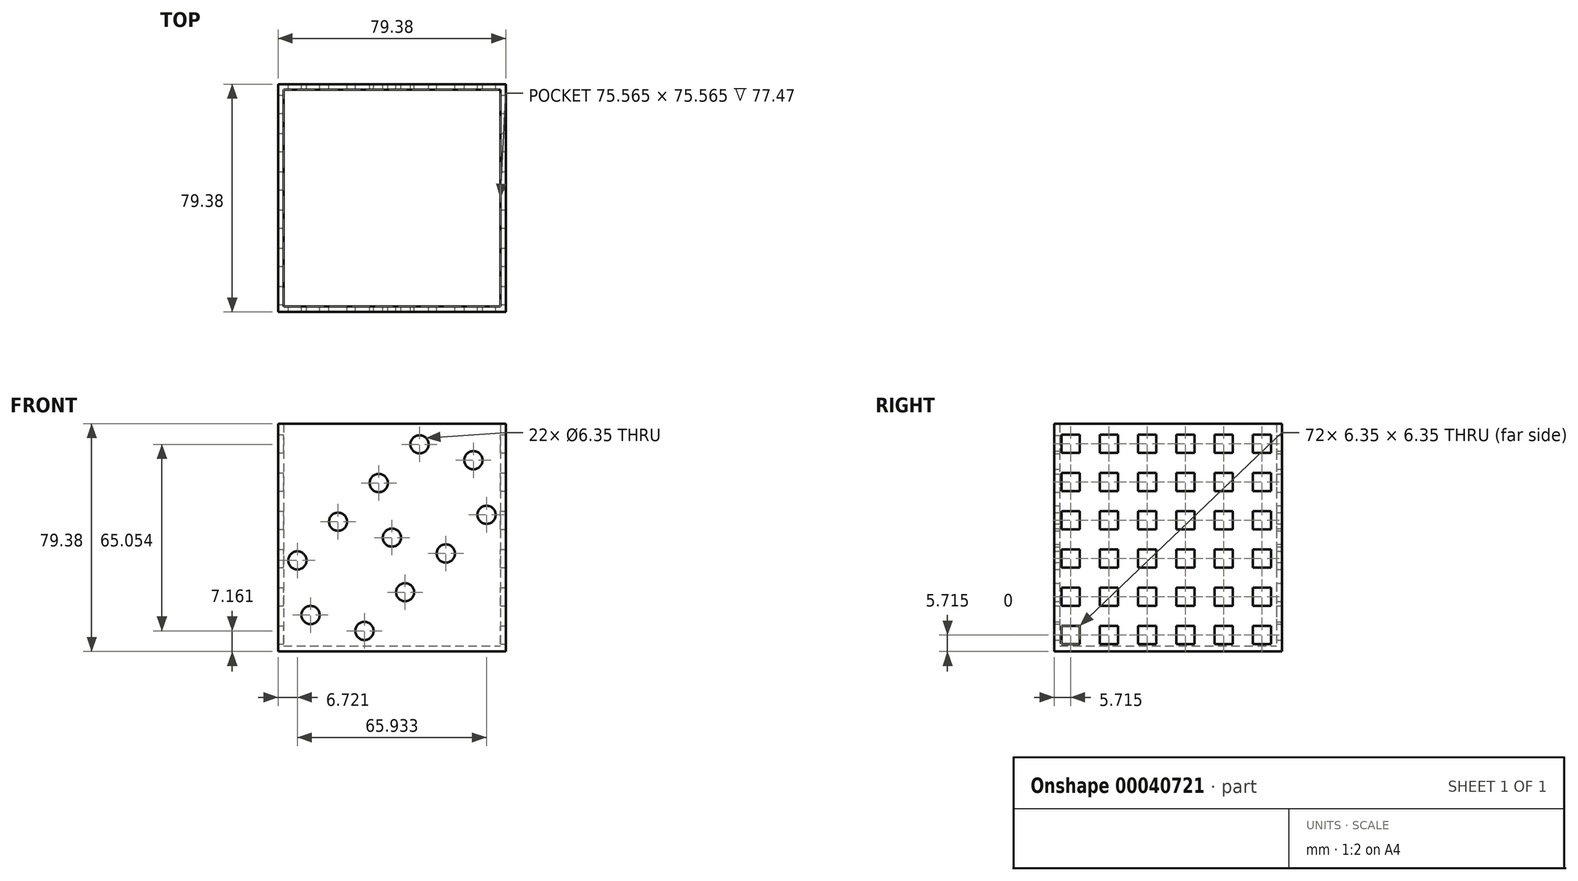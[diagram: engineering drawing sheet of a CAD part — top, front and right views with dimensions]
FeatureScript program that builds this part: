
annotation { "Feature Type Name" : "Feature", "Feature Type Description" : "" }
export const myFeature = defineFeature(function(context is Context, id is Id, definition is map)
    precondition{}
    {
        {
            var Q0;
            Q0=qCreatedBy(makeId("Top.planeOp"),FACE);
            var sketch = newSketch(context, id + "F0", { "sketchPlane" : qUnion([Q0])});
            skLineSegment(sketch, "E0.bottom", {"start": v(0, 0) * mm, "end": v(79.38, 0) * mm});
            skLineSegment(sketch, "E0.top", {"start": v(0, 79.38) * mm, "end": v(79.37, 79.38) * mm});
            skLineSegment(sketch, "E0.left", {"start": v(0, 0) * mm, "end": v(0, 79.38) * mm});
            skLineSegment(sketch, "E0.right", {"start": v(79.38, 0) * mm, "end": v(79.38, 79.38) * mm});
            skSolve(sketch);
        }
        {
            var Q0;
            Q0=makeQuery(id+"F0.imprint","IMPRINT",FACE,{"disambiguationData":[TD([[makeQuery(id+"F0.imprint","IMPRINT",EDGE,{"derivedFrom":sQuery(id+"F0.wireOp",EDGE,"E0.bottom")}),1.0]])]});
            extrude(context, id + "F1", {"entities" : qUnion([Q0]), "depth" : 79.38 * mm});
        }
        {
            var Q0;
            Q0=makeQuery(id+"F1.opExtrude","CAP_FACE",FACE,{"disambiguationData":[OSD([sQuery(id+"F0.wireOp",EDGE,"E0.bottom"),sQuery(id+"F0.wireOp",EDGE,"E0.top"),sQuery(id+"F0.wireOp",EDGE,"E0.left"),sQuery(id+"F0.wireOp",EDGE,"E0.right")])],"isStart":false});
            shell(context, id + "F2", {"entities" : qUnion([Q0]), "thickness" : 1.9 * mm});
        }
        {
            var Q0;
            Q0=makeQuery(id+"F1.opExtrude","SWEPT_FACE",FACE,{"disambiguationData":[OSD([sQuery(id+"F0.wireOp",EDGE,"E0.right")])]});
            var sketch = newSketch(context, id + "F3", { "sketchPlane" : qUnion([Q0])});
            skLineSegment(sketch, "E1.bottom", {"start": v(2.54, 8.9) * mm, "end": v(8.9, 8.9) * mm});
            skLineSegment(sketch, "E1.top", {"start": v(2.54, 2.54) * mm, "end": v(8.9, 2.54) * mm});
            skLineSegment(sketch, "E1.left", {"start": v(2.54, 8.9) * mm, "end": v(2.54, 2.54) * mm});
            skLineSegment(sketch, "E1.right", {"start": v(8.9, 8.9) * mm, "end": v(8.9, 2.54) * mm});
            skLineSegment(sketch, "E2.0.1.0", {"start": v(2.54, 22.23) * mm, "end": v(8.9, 22.23) * mm});
            skLineSegment(sketch, "E2.0.1.1", {"start": v(2.54, 22.23) * mm, "end": v(2.54, 15.88) * mm});
            skLineSegment(sketch, "E2.0.1.2", {"start": v(2.54, 15.88) * mm, "end": v(8.9, 15.88) * mm});
            skLineSegment(sketch, "E2.0.1.3", {"start": v(8.9, 22.23) * mm, "end": v(8.9, 15.88) * mm});
            skLineSegment(sketch, "E2.0.2.0", {"start": v(2.54, 35.56) * mm, "end": v(8.9, 35.56) * mm});
            skLineSegment(sketch, "E2.0.2.1", {"start": v(2.54, 35.56) * mm, "end": v(2.54, 29.21) * mm});
            skLineSegment(sketch, "E2.0.2.2", {"start": v(2.54, 29.21) * mm, "end": v(8.9, 29.21) * mm});
            skLineSegment(sketch, "E2.0.2.3", {"start": v(8.9, 35.56) * mm, "end": v(8.9, 29.21) * mm});
            skLineSegment(sketch, "E2.0.3.0", {"start": v(2.54, 48.9) * mm, "end": v(8.9, 48.9) * mm});
            skLineSegment(sketch, "E2.0.3.1", {"start": v(2.54, 48.9) * mm, "end": v(2.54, 42.55) * mm});
            skLineSegment(sketch, "E2.0.3.2", {"start": v(2.54, 42.55) * mm, "end": v(8.9, 42.55) * mm});
            skLineSegment(sketch, "E2.0.3.3", {"start": v(8.9, 48.9) * mm, "end": v(8.9, 42.55) * mm});
            skLineSegment(sketch, "E2.0.4.0", {"start": v(2.54, 62.23) * mm, "end": v(8.9, 62.23) * mm});
            skLineSegment(sketch, "E2.0.4.1", {"start": v(2.54, 62.23) * mm, "end": v(2.54, 55.88) * mm});
            skLineSegment(sketch, "E2.0.4.2", {"start": v(2.54, 55.88) * mm, "end": v(8.9, 55.88) * mm});
            skLineSegment(sketch, "E2.0.4.3", {"start": v(8.9, 62.23) * mm, "end": v(8.9, 55.88) * mm});
            skLineSegment(sketch, "E2.0.5.0", {"start": v(2.54, 75.56) * mm, "end": v(8.9, 75.56) * mm});
            skLineSegment(sketch, "E2.0.5.1", {"start": v(2.54, 75.56) * mm, "end": v(2.54, 69.22) * mm});
            skLineSegment(sketch, "E2.0.5.2", {"start": v(2.54, 69.22) * mm, "end": v(8.9, 69.22) * mm});
            skLineSegment(sketch, "E2.0.5.3", {"start": v(8.9, 75.56) * mm, "end": v(8.9, 69.22) * mm});
            skLineSegment(sketch, "E2.1.0.0", {"start": v(15.88, 8.9) * mm, "end": v(22.23, 8.9) * mm});
            skLineSegment(sketch, "E2.1.0.1", {"start": v(15.88, 8.9) * mm, "end": v(15.88, 2.54) * mm});
            skLineSegment(sketch, "E2.1.0.2", {"start": v(15.88, 2.54) * mm, "end": v(22.23, 2.54) * mm});
            skLineSegment(sketch, "E2.1.0.3", {"start": v(22.23, 8.9) * mm, "end": v(22.23, 2.54) * mm});
            skLineSegment(sketch, "E2.1.1.0", {"start": v(15.88, 22.23) * mm, "end": v(22.23, 22.23) * mm});
            skLineSegment(sketch, "E2.1.1.1", {"start": v(15.88, 22.23) * mm, "end": v(15.88, 15.88) * mm});
            skLineSegment(sketch, "E2.1.1.2", {"start": v(15.88, 15.88) * mm, "end": v(22.23, 15.88) * mm});
            skLineSegment(sketch, "E2.1.1.3", {"start": v(22.23, 22.23) * mm, "end": v(22.23, 15.88) * mm});
            skLineSegment(sketch, "E2.1.2.0", {"start": v(15.88, 35.56) * mm, "end": v(22.23, 35.56) * mm});
            skLineSegment(sketch, "E2.1.2.1", {"start": v(15.88, 35.56) * mm, "end": v(15.88, 29.21) * mm});
            skLineSegment(sketch, "E2.1.2.2", {"start": v(15.88, 29.21) * mm, "end": v(22.23, 29.21) * mm});
            skLineSegment(sketch, "E2.1.2.3", {"start": v(22.23, 35.56) * mm, "end": v(22.23, 29.21) * mm});
            skLineSegment(sketch, "E2.1.3.0", {"start": v(15.88, 48.9) * mm, "end": v(22.23, 48.9) * mm});
            skLineSegment(sketch, "E2.1.3.1", {"start": v(15.88, 48.9) * mm, "end": v(15.88, 42.55) * mm});
            skLineSegment(sketch, "E2.1.3.2", {"start": v(15.88, 42.55) * mm, "end": v(22.23, 42.55) * mm});
            skLineSegment(sketch, "E2.1.3.3", {"start": v(22.23, 48.9) * mm, "end": v(22.23, 42.55) * mm});
            skLineSegment(sketch, "E2.1.4.0", {"start": v(15.88, 62.23) * mm, "end": v(22.23, 62.23) * mm});
            skLineSegment(sketch, "E2.1.4.1", {"start": v(15.88, 62.23) * mm, "end": v(15.88, 55.88) * mm});
            skLineSegment(sketch, "E2.1.4.2", {"start": v(15.88, 55.88) * mm, "end": v(22.23, 55.88) * mm});
            skLineSegment(sketch, "E2.1.4.3", {"start": v(22.23, 62.23) * mm, "end": v(22.23, 55.88) * mm});
            skLineSegment(sketch, "E2.1.5.0", {"start": v(15.88, 75.56) * mm, "end": v(22.23, 75.56) * mm});
            skLineSegment(sketch, "E2.1.5.1", {"start": v(15.88, 75.56) * mm, "end": v(15.88, 69.22) * mm});
            skLineSegment(sketch, "E2.1.5.2", {"start": v(15.88, 69.22) * mm, "end": v(22.23, 69.22) * mm});
            skLineSegment(sketch, "E2.1.5.3", {"start": v(22.23, 75.56) * mm, "end": v(22.23, 69.22) * mm});
            skLineSegment(sketch, "E2.2.0.0", {"start": v(29.21, 8.9) * mm, "end": v(35.56, 8.9) * mm});
            skLineSegment(sketch, "E2.2.0.1", {"start": v(29.21, 8.9) * mm, "end": v(29.21, 2.54) * mm});
            skLineSegment(sketch, "E2.2.0.2", {"start": v(29.21, 2.54) * mm, "end": v(35.56, 2.54) * mm});
            skLineSegment(sketch, "E2.2.0.3", {"start": v(35.56, 8.9) * mm, "end": v(35.56, 2.54) * mm});
            skLineSegment(sketch, "E2.2.1.0", {"start": v(29.21, 22.23) * mm, "end": v(35.56, 22.23) * mm});
            skLineSegment(sketch, "E2.2.1.1", {"start": v(29.21, 22.23) * mm, "end": v(29.21, 15.88) * mm});
            skLineSegment(sketch, "E2.2.1.2", {"start": v(29.21, 15.88) * mm, "end": v(35.56, 15.88) * mm});
            skLineSegment(sketch, "E2.2.1.3", {"start": v(35.56, 22.23) * mm, "end": v(35.56, 15.88) * mm});
            skLineSegment(sketch, "E2.2.2.0", {"start": v(29.21, 35.56) * mm, "end": v(35.56, 35.56) * mm});
            skLineSegment(sketch, "E2.2.2.1", {"start": v(29.21, 35.56) * mm, "end": v(29.21, 29.21) * mm});
            skLineSegment(sketch, "E2.2.2.2", {"start": v(29.21, 29.21) * mm, "end": v(35.56, 29.21) * mm});
            skLineSegment(sketch, "E2.2.2.3", {"start": v(35.56, 35.56) * mm, "end": v(35.56, 29.21) * mm});
            skLineSegment(sketch, "E2.2.3.0", {"start": v(29.21, 48.9) * mm, "end": v(35.56, 48.9) * mm});
            skLineSegment(sketch, "E2.2.3.1", {"start": v(29.21, 48.9) * mm, "end": v(29.21, 42.55) * mm});
            skLineSegment(sketch, "E2.2.3.2", {"start": v(29.21, 42.55) * mm, "end": v(35.56, 42.55) * mm});
            skLineSegment(sketch, "E2.2.3.3", {"start": v(35.56, 48.9) * mm, "end": v(35.56, 42.55) * mm});
            skLineSegment(sketch, "E2.2.4.0", {"start": v(29.21, 62.23) * mm, "end": v(35.56, 62.23) * mm});
            skLineSegment(sketch, "E2.2.4.1", {"start": v(29.21, 62.23) * mm, "end": v(29.21, 55.88) * mm});
            skLineSegment(sketch, "E2.2.4.2", {"start": v(29.21, 55.88) * mm, "end": v(35.56, 55.88) * mm});
            skLineSegment(sketch, "E2.2.4.3", {"start": v(35.56, 62.23) * mm, "end": v(35.56, 55.88) * mm});
            skLineSegment(sketch, "E2.2.5.0", {"start": v(29.21, 75.56) * mm, "end": v(35.56, 75.56) * mm});
            skLineSegment(sketch, "E2.2.5.1", {"start": v(29.21, 75.56) * mm, "end": v(29.21, 69.22) * mm});
            skLineSegment(sketch, "E2.2.5.2", {"start": v(29.21, 69.22) * mm, "end": v(35.56, 69.22) * mm});
            skLineSegment(sketch, "E2.2.5.3", {"start": v(35.56, 75.56) * mm, "end": v(35.56, 69.22) * mm});
            skLineSegment(sketch, "E2.3.0.0", {"start": v(42.55, 8.9) * mm, "end": v(48.9, 8.9) * mm});
            skLineSegment(sketch, "E2.3.0.1", {"start": v(42.55, 8.9) * mm, "end": v(42.55, 2.54) * mm});
            skLineSegment(sketch, "E2.3.0.2", {"start": v(42.55, 2.54) * mm, "end": v(48.9, 2.54) * mm});
            skLineSegment(sketch, "E2.3.0.3", {"start": v(48.9, 8.9) * mm, "end": v(48.9, 2.54) * mm});
            skLineSegment(sketch, "E2.3.1.0", {"start": v(42.55, 22.23) * mm, "end": v(48.9, 22.23) * mm});
            skLineSegment(sketch, "E2.3.1.1", {"start": v(42.55, 22.23) * mm, "end": v(42.55, 15.88) * mm});
            skLineSegment(sketch, "E2.3.1.2", {"start": v(42.55, 15.88) * mm, "end": v(48.9, 15.88) * mm});
            skLineSegment(sketch, "E2.3.1.3", {"start": v(48.9, 22.23) * mm, "end": v(48.9, 15.88) * mm});
            skLineSegment(sketch, "E2.3.2.0", {"start": v(42.55, 35.56) * mm, "end": v(48.9, 35.56) * mm});
            skLineSegment(sketch, "E2.3.2.1", {"start": v(42.55, 35.56) * mm, "end": v(42.55, 29.21) * mm});
            skLineSegment(sketch, "E2.3.2.2", {"start": v(42.55, 29.21) * mm, "end": v(48.9, 29.21) * mm});
            skLineSegment(sketch, "E2.3.2.3", {"start": v(48.9, 35.56) * mm, "end": v(48.9, 29.21) * mm});
            skLineSegment(sketch, "E2.3.3.0", {"start": v(42.55, 48.9) * mm, "end": v(48.9, 48.9) * mm});
            skLineSegment(sketch, "E2.3.3.1", {"start": v(42.55, 48.9) * mm, "end": v(42.55, 42.55) * mm});
            skLineSegment(sketch, "E2.3.3.2", {"start": v(42.55, 42.55) * mm, "end": v(48.9, 42.55) * mm});
            skLineSegment(sketch, "E2.3.3.3", {"start": v(48.9, 48.9) * mm, "end": v(48.9, 42.55) * mm});
            skLineSegment(sketch, "E2.3.4.0", {"start": v(42.55, 62.23) * mm, "end": v(48.9, 62.23) * mm});
            skLineSegment(sketch, "E2.3.4.1", {"start": v(42.55, 62.23) * mm, "end": v(42.55, 55.88) * mm});
            skLineSegment(sketch, "E2.3.4.2", {"start": v(42.55, 55.88) * mm, "end": v(48.9, 55.88) * mm});
            skLineSegment(sketch, "E2.3.4.3", {"start": v(48.9, 62.23) * mm, "end": v(48.9, 55.88) * mm});
            skLineSegment(sketch, "E2.3.5.0", {"start": v(42.55, 75.56) * mm, "end": v(48.9, 75.56) * mm});
            skLineSegment(sketch, "E2.3.5.1", {"start": v(42.55, 75.56) * mm, "end": v(42.55, 69.22) * mm});
            skLineSegment(sketch, "E2.3.5.2", {"start": v(42.55, 69.22) * mm, "end": v(48.9, 69.22) * mm});
            skLineSegment(sketch, "E2.3.5.3", {"start": v(48.9, 75.56) * mm, "end": v(48.9, 69.22) * mm});
            skLineSegment(sketch, "E2.4.0.0", {"start": v(55.88, 8.9) * mm, "end": v(62.23, 8.9) * mm});
            skLineSegment(sketch, "E2.4.0.1", {"start": v(55.88, 8.9) * mm, "end": v(55.88, 2.54) * mm});
            skLineSegment(sketch, "E2.4.0.2", {"start": v(55.88, 2.54) * mm, "end": v(62.23, 2.54) * mm});
            skLineSegment(sketch, "E2.4.0.3", {"start": v(62.23, 8.9) * mm, "end": v(62.23, 2.54) * mm});
            skLineSegment(sketch, "E2.4.1.0", {"start": v(55.88, 22.23) * mm, "end": v(62.23, 22.23) * mm});
            skLineSegment(sketch, "E2.4.1.1", {"start": v(55.88, 22.23) * mm, "end": v(55.88, 15.88) * mm});
            skLineSegment(sketch, "E2.4.1.2", {"start": v(55.88, 15.88) * mm, "end": v(62.23, 15.88) * mm});
            skLineSegment(sketch, "E2.4.1.3", {"start": v(62.23, 22.23) * mm, "end": v(62.23, 15.88) * mm});
            skLineSegment(sketch, "E2.4.2.0", {"start": v(55.88, 35.56) * mm, "end": v(62.23, 35.56) * mm});
            skLineSegment(sketch, "E2.4.2.1", {"start": v(55.88, 35.56) * mm, "end": v(55.88, 29.21) * mm});
            skLineSegment(sketch, "E2.4.2.2", {"start": v(55.88, 29.21) * mm, "end": v(62.23, 29.21) * mm});
            skLineSegment(sketch, "E2.4.2.3", {"start": v(62.23, 35.56) * mm, "end": v(62.23, 29.21) * mm});
            skLineSegment(sketch, "E2.4.3.0", {"start": v(55.88, 48.9) * mm, "end": v(62.23, 48.9) * mm});
            skLineSegment(sketch, "E2.4.3.1", {"start": v(55.88, 48.9) * mm, "end": v(55.88, 42.55) * mm});
            skLineSegment(sketch, "E2.4.3.2", {"start": v(55.88, 42.55) * mm, "end": v(62.23, 42.55) * mm});
            skLineSegment(sketch, "E2.4.3.3", {"start": v(62.23, 48.9) * mm, "end": v(62.23, 42.55) * mm});
            skLineSegment(sketch, "E2.4.4.0", {"start": v(55.88, 62.23) * mm, "end": v(62.23, 62.23) * mm});
            skLineSegment(sketch, "E2.4.4.1", {"start": v(55.88, 62.23) * mm, "end": v(55.88, 55.88) * mm});
            skLineSegment(sketch, "E2.4.4.2", {"start": v(55.88, 55.88) * mm, "end": v(62.23, 55.88) * mm});
            skLineSegment(sketch, "E2.4.4.3", {"start": v(62.23, 62.23) * mm, "end": v(62.23, 55.88) * mm});
            skLineSegment(sketch, "E2.4.5.0", {"start": v(55.88, 75.56) * mm, "end": v(62.23, 75.56) * mm});
            skLineSegment(sketch, "E2.4.5.1", {"start": v(55.88, 75.56) * mm, "end": v(55.88, 69.22) * mm});
            skLineSegment(sketch, "E2.4.5.2", {"start": v(55.88, 69.22) * mm, "end": v(62.23, 69.22) * mm});
            skLineSegment(sketch, "E2.4.5.3", {"start": v(62.23, 75.56) * mm, "end": v(62.23, 69.22) * mm});
            skLineSegment(sketch, "E2.5.0.0", {"start": v(69.22, 8.9) * mm, "end": v(75.56, 8.9) * mm});
            skLineSegment(sketch, "E2.5.0.1", {"start": v(69.22, 8.9) * mm, "end": v(69.22, 2.54) * mm});
            skLineSegment(sketch, "E2.5.0.2", {"start": v(69.22, 2.54) * mm, "end": v(75.57, 2.54) * mm});
            skLineSegment(sketch, "E2.5.0.3", {"start": v(75.57, 8.9) * mm, "end": v(75.57, 2.54) * mm});
            skLineSegment(sketch, "E2.5.1.0", {"start": v(69.22, 22.23) * mm, "end": v(75.56, 22.23) * mm});
            skLineSegment(sketch, "E2.5.1.1", {"start": v(69.22, 22.23) * mm, "end": v(69.22, 15.88) * mm});
            skLineSegment(sketch, "E2.5.1.2", {"start": v(69.22, 15.88) * mm, "end": v(75.57, 15.88) * mm});
            skLineSegment(sketch, "E2.5.1.3", {"start": v(75.57, 22.23) * mm, "end": v(75.57, 15.88) * mm});
            skLineSegment(sketch, "E2.5.2.0", {"start": v(69.22, 35.56) * mm, "end": v(75.56, 35.56) * mm});
            skLineSegment(sketch, "E2.5.2.1", {"start": v(69.22, 35.56) * mm, "end": v(69.22, 29.21) * mm});
            skLineSegment(sketch, "E2.5.2.2", {"start": v(69.22, 29.21) * mm, "end": v(75.57, 29.21) * mm});
            skLineSegment(sketch, "E2.5.2.3", {"start": v(75.57, 35.56) * mm, "end": v(75.57, 29.21) * mm});
            skLineSegment(sketch, "E2.5.3.0", {"start": v(69.22, 48.9) * mm, "end": v(75.56, 48.9) * mm});
            skLineSegment(sketch, "E2.5.3.1", {"start": v(69.22, 48.9) * mm, "end": v(69.22, 42.55) * mm});
            skLineSegment(sketch, "E2.5.3.2", {"start": v(69.22, 42.55) * mm, "end": v(75.57, 42.55) * mm});
            skLineSegment(sketch, "E2.5.3.3", {"start": v(75.57, 48.9) * mm, "end": v(75.57, 42.55) * mm});
            skLineSegment(sketch, "E2.5.4.0", {"start": v(69.22, 62.23) * mm, "end": v(75.56, 62.23) * mm});
            skLineSegment(sketch, "E2.5.4.1", {"start": v(69.22, 62.23) * mm, "end": v(69.22, 55.88) * mm});
            skLineSegment(sketch, "E2.5.4.2", {"start": v(69.22, 55.88) * mm, "end": v(75.57, 55.88) * mm});
            skLineSegment(sketch, "E2.5.4.3", {"start": v(75.57, 62.23) * mm, "end": v(75.57, 55.88) * mm});
            skLineSegment(sketch, "E2.5.5.0", {"start": v(69.22, 75.56) * mm, "end": v(75.56, 75.56) * mm});
            skLineSegment(sketch, "E2.5.5.1", {"start": v(69.22, 75.56) * mm, "end": v(69.22, 69.22) * mm});
            skLineSegment(sketch, "E2.5.5.2", {"start": v(69.22, 69.22) * mm, "end": v(75.57, 69.22) * mm});
            skLineSegment(sketch, "E2.5.5.3", {"start": v(75.57, 75.56) * mm, "end": v(75.57, 69.22) * mm});
            skLineSegment(sketch, "E2.direction1", {"start": v(2.54, 8.9) * mm, "end": v(15.88, 8.9) * mm, "construction": true});
            skLineSegment(sketch, "E2.direction2", {"start": v(2.54, 8.9) * mm, "end": v(2.54, 22.23) * mm, "construction": true});
            skSolve(sketch);
        }
        {
            var Q0;
            Q0=makeQuery(id+"F3.imprint","IMPRINT",FACE,{"disambiguationData":[TD([[makeQuery(id+"F3.imprint","IMPRINT",EDGE,{"derivedFrom":sQuery(id+"F3.wireOp",EDGE,"E2.0.5.0")}),-1.0]])]});
            var Q1;
            Q1=makeQuery(id+"F3.imprint","IMPRINT",FACE,{"disambiguationData":[TD([[makeQuery(id+"F3.imprint","IMPRINT",EDGE,{"derivedFrom":sQuery(id+"F3.wireOp",EDGE,"E2.1.5.0")}),-1.0]])]});
            var Q2;
            Q2=makeQuery(id+"F3.imprint","IMPRINT",FACE,{"disambiguationData":[TD([[makeQuery(id+"F3.imprint","IMPRINT",EDGE,{"derivedFrom":sQuery(id+"F3.wireOp",EDGE,"E2.2.5.0")}),-1.0]])]});
            var Q3;
            Q3=makeQuery(id+"F3.imprint","IMPRINT",FACE,{"disambiguationData":[TD([[makeQuery(id+"F3.imprint","IMPRINT",EDGE,{"derivedFrom":sQuery(id+"F3.wireOp",EDGE,"E2.3.5.0")}),-1.0]])]});
            var Q4;
            Q4=makeQuery(id+"F3.imprint","IMPRINT",FACE,{"disambiguationData":[TD([[makeQuery(id+"F3.imprint","IMPRINT",EDGE,{"derivedFrom":sQuery(id+"F3.wireOp",EDGE,"E2.4.5.0")}),-1.0]])]});
            var Q5;
            Q5=makeQuery(id+"F3.imprint","IMPRINT",FACE,{"disambiguationData":[TD([[makeQuery(id+"F3.imprint","IMPRINT",EDGE,{"derivedFrom":sQuery(id+"F3.wireOp",EDGE,"E2.5.5.0")}),-1.0]])]});
            var Q6;
            Q6=makeQuery(id+"F3.imprint","IMPRINT",FACE,{"disambiguationData":[TD([[makeQuery(id+"F3.imprint","IMPRINT",EDGE,{"derivedFrom":sQuery(id+"F3.wireOp",EDGE,"E2.5.4.0")}),-1.0]])]});
            var Q7;
            Q7=makeQuery(id+"F3.imprint","IMPRINT",FACE,{"disambiguationData":[TD([[makeQuery(id+"F3.imprint","IMPRINT",EDGE,{"derivedFrom":sQuery(id+"F3.wireOp",EDGE,"E2.4.4.0")}),-1.0]])]});
            var Q8;
            Q8=makeQuery(id+"F3.imprint","IMPRINT",FACE,{"disambiguationData":[TD([[makeQuery(id+"F3.imprint","IMPRINT",EDGE,{"derivedFrom":sQuery(id+"F3.wireOp",EDGE,"E2.3.4.0")}),-1.0]])]});
            var Q9;
            Q9=makeQuery(id+"F3.imprint","IMPRINT",FACE,{"disambiguationData":[TD([[makeQuery(id+"F3.imprint","IMPRINT",EDGE,{"derivedFrom":sQuery(id+"F3.wireOp",EDGE,"E2.2.4.0")}),-1.0]])]});
            var Q10;
            Q10=makeQuery(id+"F3.imprint","IMPRINT",FACE,{"disambiguationData":[TD([[makeQuery(id+"F3.imprint","IMPRINT",EDGE,{"derivedFrom":sQuery(id+"F3.wireOp",EDGE,"E2.1.4.0")}),-1.0]])]});
            var Q11;
            Q11=makeQuery(id+"F3.imprint","IMPRINT",FACE,{"disambiguationData":[TD([[makeQuery(id+"F3.imprint","IMPRINT",EDGE,{"derivedFrom":sQuery(id+"F3.wireOp",EDGE,"E2.0.4.0")}),-1.0]])]});
            var Q12;
            Q12=makeQuery(id+"F3.imprint","IMPRINT",FACE,{"disambiguationData":[TD([[makeQuery(id+"F3.imprint","IMPRINT",EDGE,{"derivedFrom":sQuery(id+"F3.wireOp",EDGE,"E2.0.3.0")}),-1.0]])]});
            var Q13;
            Q13=makeQuery(id+"F3.imprint","IMPRINT",FACE,{"disambiguationData":[TD([[makeQuery(id+"F3.imprint","IMPRINT",EDGE,{"derivedFrom":sQuery(id+"F3.wireOp",EDGE,"E2.1.3.0")}),-1.0]])]});
            var Q14;
            Q14=makeQuery(id+"F3.imprint","IMPRINT",FACE,{"disambiguationData":[TD([[makeQuery(id+"F3.imprint","IMPRINT",EDGE,{"derivedFrom":sQuery(id+"F3.wireOp",EDGE,"E2.2.3.0")}),-1.0]])]});
            var Q15;
            Q15=makeQuery(id+"F3.imprint","IMPRINT",FACE,{"disambiguationData":[TD([[makeQuery(id+"F3.imprint","IMPRINT",EDGE,{"derivedFrom":sQuery(id+"F3.wireOp",EDGE,"E2.3.3.0")}),-1.0]])]});
            var Q16;
            Q16=makeQuery(id+"F3.imprint","IMPRINT",FACE,{"disambiguationData":[TD([[makeQuery(id+"F3.imprint","IMPRINT",EDGE,{"derivedFrom":sQuery(id+"F3.wireOp",EDGE,"E2.4.3.0")}),-1.0]])]});
            var Q17;
            Q17=makeQuery(id+"F3.imprint","IMPRINT",FACE,{"disambiguationData":[TD([[makeQuery(id+"F3.imprint","IMPRINT",EDGE,{"derivedFrom":sQuery(id+"F3.wireOp",EDGE,"E2.5.3.0")}),-1.0]])]});
            var Q18;
            Q18=makeQuery(id+"F3.imprint","IMPRINT",FACE,{"disambiguationData":[TD([[makeQuery(id+"F3.imprint","IMPRINT",EDGE,{"derivedFrom":sQuery(id+"F3.wireOp",EDGE,"E2.5.2.0")}),-1.0]])]});
            var Q19;
            Q19=makeQuery(id+"F3.imprint","IMPRINT",FACE,{"disambiguationData":[TD([[makeQuery(id+"F3.imprint","IMPRINT",EDGE,{"derivedFrom":sQuery(id+"F3.wireOp",EDGE,"E2.4.2.0")}),-1.0]])]});
            var Q20;
            Q20=makeQuery(id+"F3.imprint","IMPRINT",FACE,{"disambiguationData":[TD([[makeQuery(id+"F3.imprint","IMPRINT",EDGE,{"derivedFrom":sQuery(id+"F3.wireOp",EDGE,"E2.3.2.0")}),-1.0]])]});
            var Q21;
            Q21=makeQuery(id+"F3.imprint","IMPRINT",FACE,{"disambiguationData":[TD([[makeQuery(id+"F3.imprint","IMPRINT",EDGE,{"derivedFrom":sQuery(id+"F3.wireOp",EDGE,"E2.2.2.0")}),-1.0]])]});
            var Q22;
            Q22=makeQuery(id+"F3.imprint","IMPRINT",FACE,{"disambiguationData":[TD([[makeQuery(id+"F3.imprint","IMPRINT",EDGE,{"derivedFrom":sQuery(id+"F3.wireOp",EDGE,"E2.1.2.0")}),-1.0]])]});
            var Q23;
            Q23=makeQuery(id+"F3.imprint","IMPRINT",FACE,{"disambiguationData":[TD([[makeQuery(id+"F3.imprint","IMPRINT",EDGE,{"derivedFrom":sQuery(id+"F3.wireOp",EDGE,"E2.0.2.0")}),-1.0]])]});
            var Q24;
            Q24=makeQuery(id+"F3.imprint","IMPRINT",FACE,{"disambiguationData":[TD([[makeQuery(id+"F3.imprint","IMPRINT",EDGE,{"derivedFrom":sQuery(id+"F3.wireOp",EDGE,"E2.0.1.0")}),-1.0]])]});
            var Q25;
            Q25=makeQuery(id+"F3.imprint","IMPRINT",FACE,{"disambiguationData":[TD([[makeQuery(id+"F3.imprint","IMPRINT",EDGE,{"derivedFrom":sQuery(id+"F3.wireOp",EDGE,"E2.1.1.0")}),-1.0]])]});
            var Q26;
            Q26=makeQuery(id+"F3.imprint","IMPRINT",FACE,{"disambiguationData":[TD([[makeQuery(id+"F3.imprint","IMPRINT",EDGE,{"derivedFrom":sQuery(id+"F3.wireOp",EDGE,"E2.2.1.0")}),-1.0]])]});
            var Q27;
            Q27=makeQuery(id+"F3.imprint","IMPRINT",FACE,{"disambiguationData":[TD([[makeQuery(id+"F3.imprint","IMPRINT",EDGE,{"derivedFrom":sQuery(id+"F3.wireOp",EDGE,"E2.3.1.0")}),-1.0]])]});
            var Q28;
            Q28=makeQuery(id+"F3.imprint","IMPRINT",FACE,{"disambiguationData":[TD([[makeQuery(id+"F3.imprint","IMPRINT",EDGE,{"derivedFrom":sQuery(id+"F3.wireOp",EDGE,"E2.4.1.0")}),-1.0]])]});
            var Q29;
            Q29=makeQuery(id+"F3.imprint","IMPRINT",FACE,{"disambiguationData":[TD([[makeQuery(id+"F3.imprint","IMPRINT",EDGE,{"derivedFrom":sQuery(id+"F3.wireOp",EDGE,"E2.5.1.0")}),-1.0]])]});
            var Q30;
            Q30=makeQuery(id+"F3.imprint","IMPRINT",FACE,{"disambiguationData":[TD([[makeQuery(id+"F3.imprint","IMPRINT",EDGE,{"derivedFrom":sQuery(id+"F3.wireOp",EDGE,"E2.5.0.0")}),-1.0]])]});
            var Q31;
            Q31=makeQuery(id+"F3.imprint","IMPRINT",FACE,{"disambiguationData":[TD([[makeQuery(id+"F3.imprint","IMPRINT",EDGE,{"derivedFrom":sQuery(id+"F3.wireOp",EDGE,"E2.4.0.0")}),-1.0]])]});
            var Q32;
            Q32=makeQuery(id+"F3.imprint","IMPRINT",FACE,{"disambiguationData":[TD([[makeQuery(id+"F3.imprint","IMPRINT",EDGE,{"derivedFrom":sQuery(id+"F3.wireOp",EDGE,"E2.3.0.0")}),-1.0]])]});
            var Q33;
            Q33=makeQuery(id+"F3.imprint","IMPRINT",FACE,{"disambiguationData":[TD([[makeQuery(id+"F3.imprint","IMPRINT",EDGE,{"derivedFrom":sQuery(id+"F3.wireOp",EDGE,"E2.2.0.0")}),-1.0]])]});
            var Q34;
            Q34=makeQuery(id+"F3.imprint","IMPRINT",FACE,{"disambiguationData":[TD([[makeQuery(id+"F3.imprint","IMPRINT",EDGE,{"derivedFrom":sQuery(id+"F3.wireOp",EDGE,"E2.1.0.0")}),-1.0]])]});
            var Q35;
            Q35=makeQuery(id+"F3.imprint","IMPRINT",FACE,{"disambiguationData":[TD([[makeQuery(id+"F3.imprint","IMPRINT",EDGE,{"derivedFrom":sQuery(id+"F3.wireOp",EDGE,"E1.bottom")}),-1.0]])]});
            extrude(context, id + "F4", {"entities" : qUnion([Q0, Q1, Q2, Q3, Q4, Q5, Q6, Q7, Q8, Q9, Q10, Q11, Q12, Q13, Q14, Q15, Q16, Q17, Q18, Q19, Q20, Q21, Q22, Q23, Q24, Q25, Q26, Q27, Q28, Q29, Q30, Q31, Q32, Q33, Q34, Q35]), "operationType" : NewBodyOperationType.REMOVE, "endBound" : BoundingType.THROUGH_ALL, "oppositeDirection" : true, "depth" : 25.4 * mm});
        }
        {
            var Q0;
            Q0=makeQuery(id+"F1.opExtrude","SWEPT_FACE",FACE,{"disambiguationData":[OSD([sQuery(id+"F0.wireOp",EDGE,"E0.top")])]});
            var sketch = newSketch(context, id + "F5", { "sketchPlane" : qUnion([Q0])});
            skPoint(sketch, "E3", {"position": v(-79.38, 39.69) * mm});
            skPoint(sketch, "E4", {"position": v(-39.69, 79.38) * mm});
            skPoint(sketch, "E5", {"position": v(-39.69, 39.69) * mm});
            skCircle(sketch, "E6", {"center": v(-39.69, 39.69) * mm, "radius": 3.18 * mm});
            skCircle(sketch, "E7.1.0", {"center": v(-35.1, 58.72) * mm, "radius": 3.18 * mm});
            skCircle(sketch, "E7.2.0", {"center": v(-49.28, 72.21) * mm, "radius": 3.18 * mm});
            skCircle(sketch, "E7.3.0", {"center": v(-68.06, 66.68) * mm, "radius": 3.18 * mm});
            skCircle(sketch, "E7.4.0", {"center": v(-72.65, 47.64) * mm, "radius": 3.18 * mm});
            skCircle(sketch, "E7.5.0", {"center": v(-58.47, 34.15) * mm, "radius": 3.18 * mm});
            skPoint(sketch, "E7.center", {"position": v(-53.87, 53.18) * mm});
            skCircle(sketch, "E8.1.0", {"center": v(-44.28, 20.65) * mm, "radius": 3.18 * mm});
            skCircle(sketch, "E8.2.0", {"center": v(-30.1, 7.16) * mm, "radius": 3.18 * mm});
            skCircle(sketch, "E8.3.0", {"center": v(-11.31, 12.7) * mm, "radius": 3.18 * mm});
            skCircle(sketch, "E8.4.0", {"center": v(-6.72, 31.73) * mm, "radius": 3.18 * mm});
            skCircle(sketch, "E8.5.0", {"center": v(-20.9, 45.23) * mm, "radius": 3.18 * mm});
            skPoint(sketch, "E8.center", {"position": v(-25.5, 26.2) * mm});
            skLineSegment(sketch, "E9", {"start": v(-68.06, 66.68) * mm, "end": v(-11.31, 12.7) * mm, "construction": true});
            skSolve(sketch);
        }
        {
            var Q0;
            Q0=makeQuery(id+"F5.imprint","IMPRINT",FACE,{"disambiguationData":[TD([[makeQuery(id+"F5.imprint","IMPRINT",EDGE,{"derivedFrom":sQuery(id+"F5.wireOp",EDGE,"E7.2.0")}),1.0]])]});
            var Q1;
            Q1=makeQuery(id+"F5.imprint","IMPRINT",FACE,{"disambiguationData":[TD([[makeQuery(id+"F5.imprint","IMPRINT",EDGE,{"derivedFrom":sQuery(id+"F5.wireOp",EDGE,"E7.1.0")}),1.0]])]});
            var Q2;
            Q2=makeQuery(id+"F5.imprint","IMPRINT",FACE,{"disambiguationData":[TD([[makeQuery(id+"F5.imprint","IMPRINT",EDGE,{"derivedFrom":sQuery(id+"F5.wireOp",EDGE,"E8.5.0")}),1.0]])]});
            var Q3;
            Q3=makeQuery(id+"F5.imprint","IMPRINT",FACE,{"disambiguationData":[TD([[makeQuery(id+"F5.imprint","IMPRINT",EDGE,{"derivedFrom":sQuery(id+"F5.wireOp",EDGE,"E8.4.0")}),1.0]])]});
            var Q4;
            Q4=makeQuery(id+"F5.imprint","IMPRINT",FACE,{"disambiguationData":[TD([[makeQuery(id+"F5.imprint","IMPRINT",EDGE,{"derivedFrom":sQuery(id+"F5.wireOp",EDGE,"E8.3.0")}),1.0]])]});
            var Q5;
            Q5=makeQuery(id+"F5.imprint","IMPRINT",FACE,{"disambiguationData":[TD([[makeQuery(id+"F5.imprint","IMPRINT",EDGE,{"derivedFrom":sQuery(id+"F5.wireOp",EDGE,"E8.2.0")}),1.0]])]});
            var Q6;
            Q6=makeQuery(id+"F5.imprint","IMPRINT",FACE,{"disambiguationData":[TD([[makeQuery(id+"F5.imprint","IMPRINT",EDGE,{"derivedFrom":sQuery(id+"F5.wireOp",EDGE,"E8.1.0")}),1.0]])]});
            var Q7;
            Q7=makeQuery(id+"F5.imprint","IMPRINT",FACE,{"disambiguationData":[TD([[makeQuery(id+"F5.imprint","IMPRINT",EDGE,{"derivedFrom":sQuery(id+"F5.wireOp",EDGE,"E7.5.0")}),1.0]])]});
            var Q8;
            Q8=makeQuery(id+"F5.imprint","IMPRINT",FACE,{"disambiguationData":[TD([[makeQuery(id+"F5.imprint","IMPRINT",EDGE,{"derivedFrom":sQuery(id+"F5.wireOp",EDGE,"E7.4.0")}),1.0]])]});
            var Q9;
            Q9=makeQuery(id+"F5.imprint","IMPRINT",FACE,{"disambiguationData":[TD([[makeQuery(id+"F5.imprint","IMPRINT",EDGE,{"derivedFrom":sQuery(id+"F5.wireOp",EDGE,"E7.3.0")}),1.0]])]});
            var Q10;
            Q10=makeQuery(id+"F5.imprint","IMPRINT",FACE,{"disambiguationData":[TD([[makeQuery(id+"F5.imprint","IMPRINT",EDGE,{"derivedFrom":sQuery(id+"F5.wireOp",EDGE,"E6")}),1.0]])]});
            extrude(context, id + "F6", {"entities" : qUnion([Q0, Q1, Q2, Q3, Q4, Q5, Q6, Q7, Q8, Q9, Q10]), "operationType" : NewBodyOperationType.REMOVE, "endBound" : BoundingType.THROUGH_ALL, "oppositeDirection" : true, "depth" : 25.4 * mm});
        }
    });
